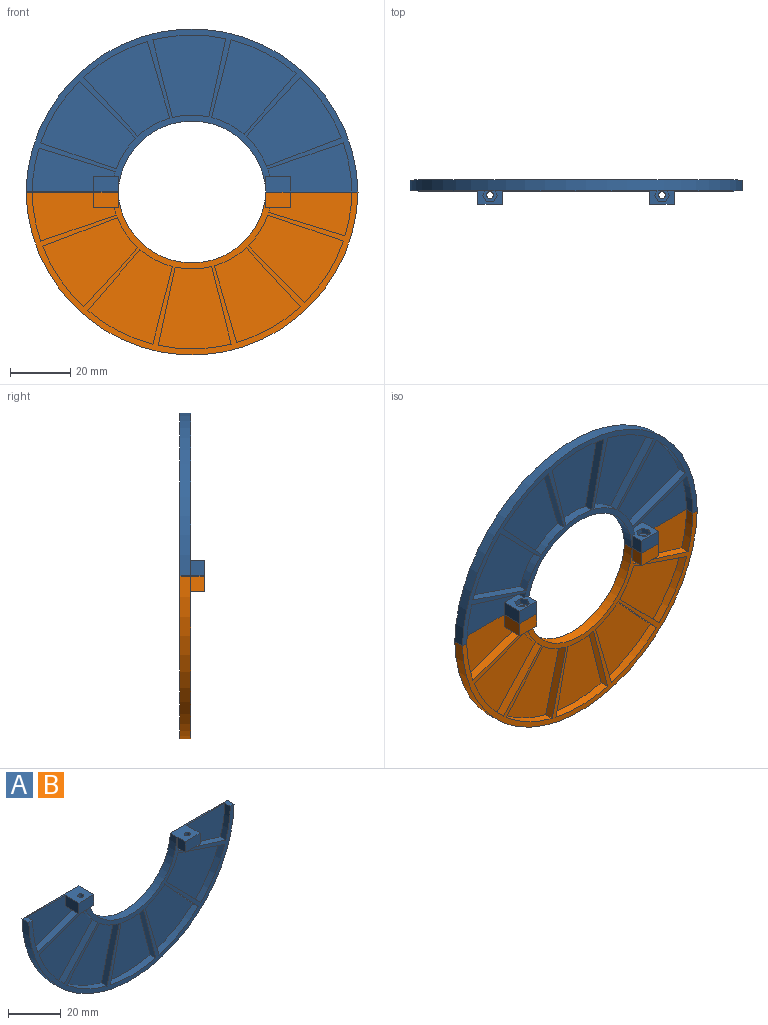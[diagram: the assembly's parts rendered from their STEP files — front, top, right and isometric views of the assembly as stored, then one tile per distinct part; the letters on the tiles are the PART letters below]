
ASSEMBLY  parts=2 mates=1
PART A: 63 faces, bbox 110x8x54 mm
  f0: plane 8x7.4mm, normal (0,0,-1), area 39.9mm2, adj f1,f20,f21,f22,f24,f25,f26,f27
  f1: plane 27.93x16.26mm, normal (0,-1,0), area 291.5mm2, adj f0,f6,f21,f48,f49,f50
  f2: plane 27.65x14.5mm, normal (0,-1,0), area 254.8mm2, adj f3,f4,f11,f46,f47,f55
  f3: plane 8x7.4mm, normal (0,0,-1), area 39.9mm2, adj f2,f9,f10,f11,f13,f14,f15,f16
  f4: plane 30.51x8mm, normal (0,0,1), area 79.4mm2, adj f2,f5,f7,f8,f9,f10,f11,f12
  f5: cylinder r=24.5mm len=48.96mm, axis (0,1,0), area 269.9mm2, adj f4,f6,f8,f57
  f6: plane 30.51x8mm, normal (0,0,1), area 79.4mm2, adj f1,f5,f7,f8,f20,f21,f22,f23
  f7: cylinder r=55mm len=109.98mm, axis (0,1,0), area 614.8mm2, adj f4,f6,f8,f57
  f8: plane 109.98x54mm, normal (0,1,0), area 3747.8mm2, adj f4,f5,f6,f7
  f9: plane 5x4.4mm, normal (-1,0,0), area 22mm2, adj f3,f4,f10,f57
  f10: plane 8x5mm, normal (0,-1,0), area 40mm2, adj f3,f4,f9,f11
  f11: plane 7.4x5mm, normal (1,0,0), area 37mm2, adj f2,f3,f4,f10
  f12: cylinder r=1.15mm len=3mm, axis (0,0,1), area 21.7mm2, adj f4,f19
  f13: plane 2.43x2mm, normal (0,1,0), area 4.8mm2, adj f3,f14,f18,f19
  f14: plane 2.1x2mm, normal (-0.87,0.5,0), area 4.8mm2, adj f3,f13,f15,f19
  f15: plane 2.1x2mm, normal (-0.87,-0.5,0), area 4.8mm2, adj f3,f14,f16,f19
  f16: plane 2.43x2mm, normal (0,-1,0), area 4.8mm2, adj f3,f15,f17,f19
  f17: plane 2.1x2mm, normal (0.87,-0.5,0), area 4.8mm2, adj f3,f16,f18,f19
  f18: plane 2.1x2mm, normal (0.87,0.5,0), area 4.8mm2, adj f3,f13,f17,f19
  f19: plane 4.85x4.2mm, normal (0,0,-1), area 11.1mm2, adj f12,f13,f14,f15,f16,f17,f18
  f20: plane 5x4.4mm, normal (1,0,0), area 22mm2, adj f0,f6,f22,f57
  f21: plane 7.4x5mm, normal (-1,0,0), area 37mm2, adj f0,f1,f6,f22
  f22: plane 8x5mm, normal (0,-1,0), area 40mm2, adj f0,f6,f20,f21
  f23: cylinder r=1.15mm len=3mm, axis (0,0,1), area 21.7mm2, adj f6,f30
  f24: plane 2.43x2mm, normal (0,1,0), area 4.8mm2, adj f0,f25,f29,f30
  f25: plane 2.1x2mm, normal (-0.87,0.5,0), area 4.8mm2, adj f0,f24,f26,f30
  f26: plane 2.1x2mm, normal (-0.87,-0.5,0), area 4.8mm2, adj f0,f25,f27,f30
  f27: plane 2.43x2mm, normal (0,-1,0), area 4.8mm2, adj f0,f26,f28,f30
  f28: plane 2.1x2mm, normal (0.87,-0.5,0), area 4.8mm2, adj f0,f27,f29,f30
  f29: plane 2.1x2mm, normal (0.87,0.5,0), area 4.8mm2, adj f0,f24,f28,f30
  f30: plane 4.85x4.2mm, normal (0,0,-1), area 11.1mm2, adj f23,f24,f25,f26,f27,f28,f29
  f31: cylinder r=26.5mm len=10.24mm, axis (0,1,0), area 36.6mm2, adj f32,f56,f57,f58
  f32: plane 25.06x8.63mm, normal (-0.33,0,-0.95), area 79.5mm2, adj f31,f33,f57,f58
  f33: cylinder r=53mm len=20.48mm, axis (0,1,0), area 73.3mm2, adj f32,f56,f57,f58
  f34: plane 25.45x7.39mm, normal (0.96,0,0.28), area 79.5mm2, adj f35,f51,f57,f62
  f35: cylinder r=26.5mm len=10.54mm, axis (0,1,0), area 36.6mm2, adj f34,f36,f57,f62
  f36: plane 19.51x17.94mm, normal (-0.74,0,-0.68), area 79.5mm2, adj f35,f51,f57,f62
  f37: plane 25.9x5.6mm, normal (0.98,0,-0.21), area 79.5mm2, adj f38,f52,f57,f61
  f38: cylinder r=26.5mm len=12.1mm, axis (0,1,0), area 36.6mm2, adj f37,f39,f57,f61
  f39: plane 25.69x6.5mm, normal (-0.97,0,-0.25), area 79.5mm2, adj f38,f52,f57,f61
  f40: plane 20.12x17.25mm, normal (0.76,0,-0.65), area 79.5mm2, adj f41,f53,f57,f60
  f41: cylinder r=26.5mm len=10.75mm, axis (0,1,0), area 36.6mm2, adj f40,f42,f57,f60
  f42: plane 25.69x6.5mm, normal (-0.97,0,0.25), area 79.5mm2, adj f41,f53,f57,f60
  f43: plane 24.74x9.5mm, normal (0.36,0,-0.93), area 79.5mm2, adj f44,f54,f57,f59
  f44: cylinder r=26.5mm len=10.01mm, axis (0,1,0), area 36.6mm2, adj f43,f45,f57,f59
  f45: plane 19.51x17.94mm, normal (-0.74,0,0.68), area 79.5mm2, adj f44,f54,f57,f59
  f46: plane 25.34x7.75mm, normal (0.29,0,0.96), area 79.5mm2, adj f2,f47,f55,f57
  f47: cylinder r=26.5mm len=3mm, axis (0,1,0), area 5.4mm2, adj f2,f3,f46,f57
  f48: cylinder r=26.5mm len=3mm, axis (0,1,0), area 8.2mm2, adj f0,f1,f49,f57
  f49: plane 25.06x8.63mm, normal (-0.33,0,0.95), area 79.5mm2, adj f1,f48,f50,f57
  f50: cylinder r=53mm len=16.26mm, axis (0,1,0), area 49.7mm2, adj f1,f6,f49,f57
  f51: cylinder r=53mm len=21.09mm, axis (0,1,0), area 73.3mm2, adj f34,f36,f57,f62
  f52: cylinder r=53mm len=24.2mm, axis (0,1,0), area 73.3mm2, adj f37,f39,f57,f61
  f53: cylinder r=53mm len=21.49mm, axis (0,1,0), area 73.3mm2, adj f40,f42,f57,f60
  f54: cylinder r=53mm len=20.02mm, axis (0,1,0), area 73.3mm2, adj f43,f45,f57,f59
  f55: cylinder r=53mm len=14.5mm, axis (0,1,0), area 44.2mm2, adj f2,f4,f46,f57
  f56: plane 18.87x18.61mm, normal (0.71,0,0.7), area 79.5mm2, adj f31,f33,f57,f58
  f57: plane 109.98x54mm, normal (0,-1,0), area 694.7mm2, adj f0,f3,f4,f5,f6,f7,f9,f20
  f58: plane 31.51x29.11mm, normal (0,-1,0), area 485.4mm2, adj f31,f32,f33,f56
  f59: plane 31.54x29.52mm, normal (0,-1,0), area 485.4mm2, adj f43,f44,f45,f54
  f60: plane 31.26x27.99mm, normal (0,-1,0), area 485.4mm2, adj f40,f41,f42,f53
  f61: plane 27.31x24.2mm, normal (0,-1,0), area 485.4mm2, adj f37,f38,f39,f52
  f62: plane 31.39x28.48mm, normal (0,-1,0), area 485.4mm2, adj f34,f35,f36,f51
PART B: same geometry as A
PLACE A rot(axis=(0,-1,0),180deg) t=(-18.45,-0.36,5.56)mm
PLACE B t=(-18.45,-0.36,7.56)mm
MATE fastened B.f12 <-> A.f23  axis (0,0,1) through (10.03,-5.36,6.56)mm
